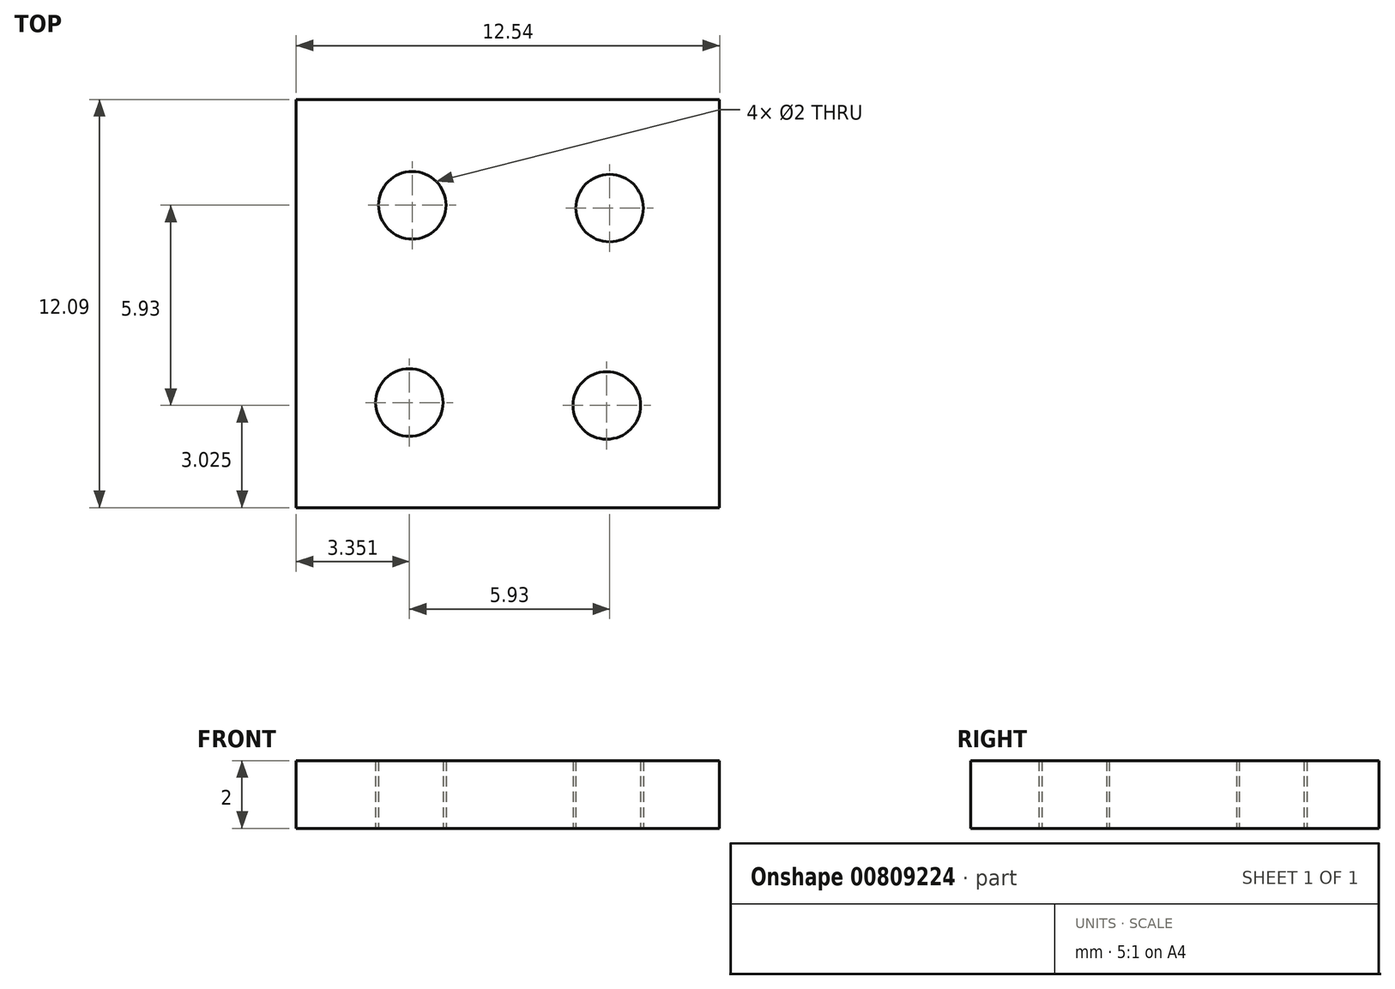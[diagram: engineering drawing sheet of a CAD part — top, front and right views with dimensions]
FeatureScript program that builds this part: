
annotation { "Feature Type Name" : "Feature", "Feature Type Description" : "" }
export const myFeature = defineFeature(function(context is Context, id is Id, definition is map)
    precondition{}
    {
        {
            var Q0;
            Q0=qCreatedBy(makeId("Top.planeOp"),FACE);
            var sketch = newSketch(context, id + "F0", { "sketchPlane" : qUnion([Q0])});
            skLineSegment(sketch, "E0.bottom", {"start": v(9.36, 2.96) * mm, "end": v(-3.18, 2.96) * mm});
            skLineSegment(sketch, "E0.top", {"start": v(9.36, -9.13) * mm, "end": v(-3.18, -9.13) * mm});
            skLineSegment(sketch, "E0.left", {"start": v(9.36, 2.96) * mm, "end": v(9.36, -9.13) * mm});
            skLineSegment(sketch, "E0.right", {"start": v(-3.18, 2.96) * mm, "end": v(-3.18, -9.13) * mm});
            skPoint(sketch, "E1", {"position": v(3.14, -3.14) * mm});
            skCircle(sketch, "E2", {"center": v(0.17, -6.02) * mm, "radius": 1 * mm});
            skCircle(sketch, "E3.1.0", {"center": v(6.02, -6.1) * mm, "radius": 1 * mm});
            skCircle(sketch, "E3.2.0", {"center": v(6.1, -0.26) * mm, "radius": 1 * mm});
            skCircle(sketch, "E3.3.0", {"center": v(0.26, -0.18) * mm, "radius": 1 * mm});
            skSolve(sketch);
        }
        {
            var Q0;
            Q0=makeQuery(id+"F0.imprint","IMPRINT",FACE,{"disambiguationData":[TD([[makeQuery(id+"F0.imprint","IMPRINT",EDGE,{"derivedFrom":sQuery(id+"F0.wireOp",EDGE,"E0.bottom")}),1.0]])]});
            extrude(context, id + "F1", {"entities" : qUnion([Q0]), "depth" : 2 * mm, "offsetDistance" : 25 * mm});
        }
    });
